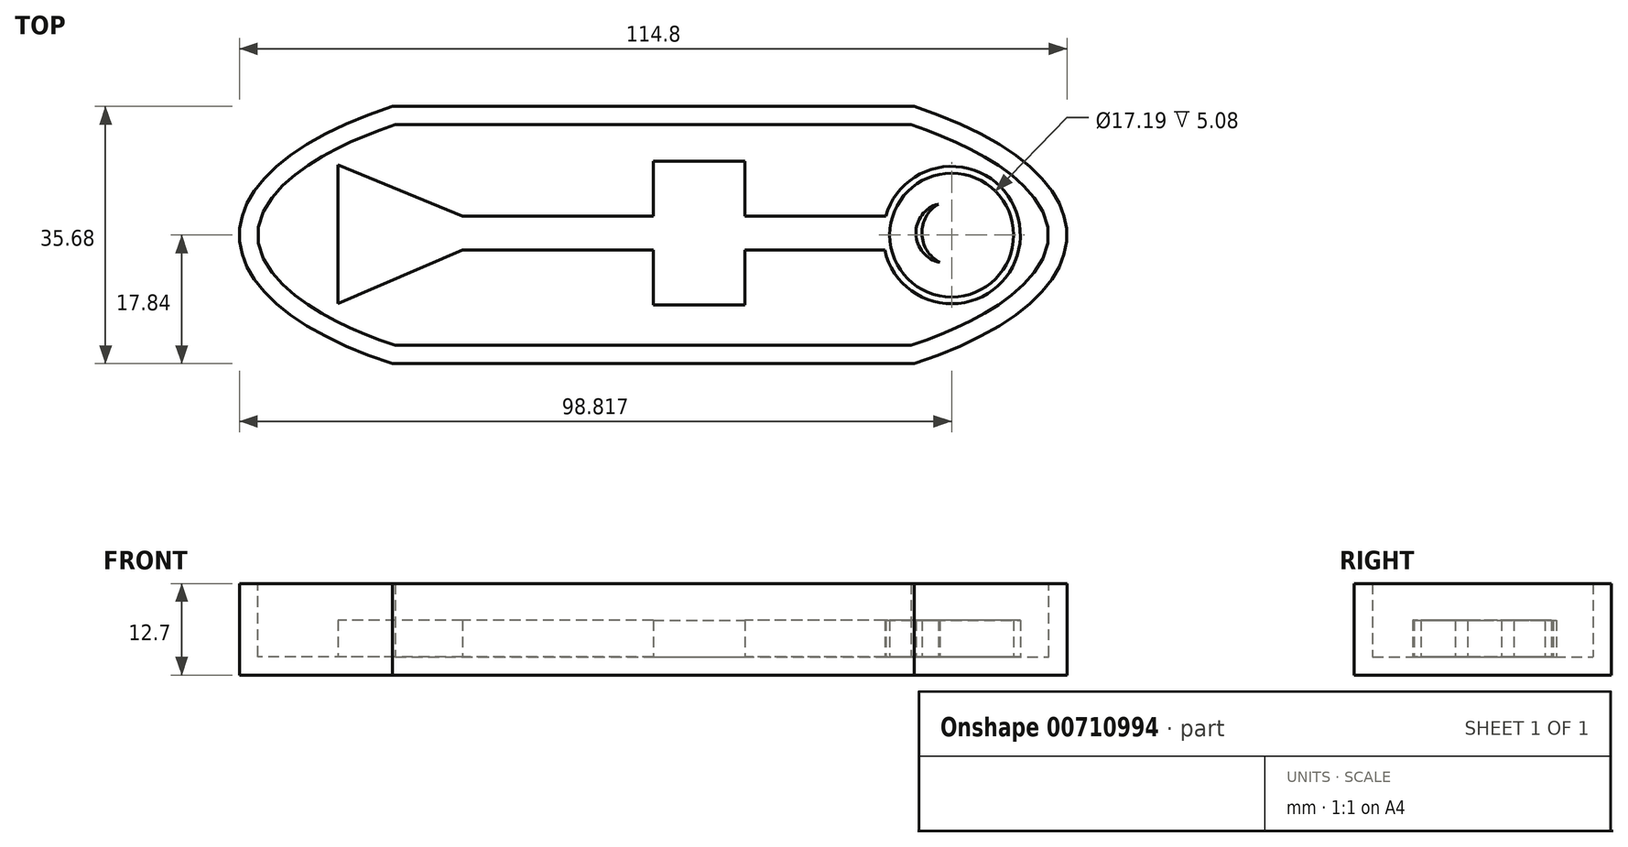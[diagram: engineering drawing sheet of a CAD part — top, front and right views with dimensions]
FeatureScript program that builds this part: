
annotation { "Feature Type Name" : "Feature", "Feature Type Description" : "" }
export const myFeature = defineFeature(function(context is Context, id is Id, definition is map)
    precondition{}
    {
        {
            var Q0;
            Q0=qCreatedBy(makeId("Top.planeOp"),FACE);
            var sketch = newSketch(context, id + "F0", { "sketchPlane" : qUnion([Q0])});
            skEllipticalArc(sketch, "E0", {});
            skLineSegment(sketch, "E1", {"start": v(-36.2, -17.84) * mm, "end": v(36.2, -17.84) * mm});
            skLineSegment(sketch, "E2", {"start": v(-36.2, 17.84) * mm, "end": v(36.2, 17.84) * mm});
            skEllipticalArc(sketch, "E3.trimOffspring", {});
            const initialGuessF0  = {"E0": [0, 0, -1, 0, 0.05740329623222351, 0.022988312008879238, 2.252938890638711, 4.030246416540875], "E3.trimOffspring": [0, 0, -1, 0, 0.05740329623222351, 0.022988312008879238, 5.394531544228505, 0.888653762951082]};
            skSetInitialGuess(sketch, initialGuessF0);
            skSolve(sketch);
        }
        {
            var Q0;
            Q0=makeQuery(id+"F0.imprint","IMPRINT",FACE,{"disambiguationData":[TD([[makeQuery(id+"F0.imprint","IMPRINT",EDGE,{"derivedFrom":sQuery(id+"F0.wireOp",EDGE,"E0")}),1.0]])]});
            extrude(context, id + "F1", {"entities" : qUnion([Q0]), "depth" : 12.7 * mm, "offsetDistance" : 25.4 * mm});
        }
        {
            var Q0;
            Q0=makeQuery(id+"F1.opExtrude","CAP_FACE",FACE,{"disambiguationData":[OSD([sQuery(id+"F0.wireOp",EDGE,"E0"),sQuery(id+"F0.wireOp",EDGE,"E1"),sQuery(id+"F0.wireOp",EDGE,"E2"),sQuery(id+"F0.wireOp",EDGE,"E3.trimOffspring")])],"isStart":false});
            shell(context, id + "F2", {"entities" : qUnion([Q0]), "thickness" : 2.54 * mm});
        }
        {
            var Q0;
            Q0=makeQuery(id+"F2.opShell","OFFSET_FACE",FACE,{"disambiguationData":[OSD([sQuery(id+"F0.wireOp",EDGE,"E0"),sQuery(id+"F0.wireOp",EDGE,"E1"),sQuery(id+"F0.wireOp",EDGE,"E2"),sQuery(id+"F0.wireOp",EDGE,"E3.trimOffspring")])]});
            var sketch = newSketch(context, id + "F3", { "sketchPlane" : qUnion([Q0])});
            skCircle(sketch, "E4", {"center": v(41.42, 0) * mm, "radius": 9.53 * mm});
            skCircle(sketch, "E5", {"center": v(41.42, 0) * mm, "radius": 8.6 * mm});
            skLineSegment(sketch, "E6", {"start": v(41.93, 8.58) * mm, "end": v(41.93, -8.58) * mm});
            skLineSegment(sketch, "E7", {"start": v(50.01, 0) * mm, "end": v(32.82, 0) * mm});
            skLineSegment(sketch, "E8", {"start": v(45.7, 7.45) * mm, "end": v(45.7, -7.45) * mm});
            skLineSegment(sketch, "E9", {"start": v(45.7, -7.45) * mm, "end": v(45.7, 7.45) * mm});
            skLineSegment(sketch, "E10", {"start": v(49.45, 3.06) * mm, "end": v(41.93, 3.06) * mm});
            skLineSegment(sketch, "E11", {"start": v(41.93, 3.06) * mm, "end": v(41.93, -3.12) * mm});
            skLineSegment(sketch, "E12", {"start": v(41.93, -3.12) * mm, "end": v(49.42, -3.12) * mm});
            skCircle(sketch, "E13", {"center": v(45.7, 3.06) * mm, "radius": 2.41 * mm});
            skCircle(sketch, "E14", {"center": v(45.7, 3.06) * mm, "radius": 1.87 * mm});
            skCircle(sketch, "E15", {"center": v(45.68, -3.12) * mm, "radius": 2.41 * mm});
            skCircle(sketch, "E16", {"center": v(45.68, -3.12) * mm, "radius": 1.87 * mm});
            skArc(sketch, "E17", {"start": v(39.57, 4.3) * mm, "mid": v(37.28, 0.2) * mm, "end": v(39.79, -3.79) * mm});
            skArc(sketch, "E18", {"start": v(39.57, 4.3) * mm, "mid": v(36.45, 0.17) * mm, "end": v(39.79, -3.79) * mm});
            skCircle(sketch, "E19", {"center": v(45.7, 3.06) * mm, "radius": 0.76 * mm});
            skCircle(sketch, "E20", {"center": v(45.68, -3.12) * mm, "radius": 0.76 * mm});
            skSolve(sketch);
        }
        {
            var Q0;
            Q0 = qSketchRegion(id + "F3", true);
            var Q1;
            {var subQ0=sQuery(id+"F3.wireOp",EDGE,"E14");var subQ1=sQuery(id+"F3.wireOp",EDGE,"E9");var subQ2=makeQuery(id+"F3.imprint","INTERSECT",VERTEX,{"disambiguationData":[OD(1.0)],"derivedFrom":[subQ1,subQ0]});Q1=makeQuery(id+"F3.imprint","IMPRINT",FACE,{"disambiguationData":[TD([[makeQuery(id+"F3.imprint","IMPRINT",EDGE,{"disambiguationData":[TD([[subQ2,-1.0]])],"derivedFrom":subQ1}),-1.0]])]});}
            var Q2;
            {var subQ0=sQuery(id+"F3.wireOp",EDGE,"E14");var subQ1=sQuery(id+"F3.wireOp",EDGE,"E9");var subQ2=makeQuery(id+"F3.imprint","INTERSECT",VERTEX,{"disambiguationData":[OD(1.0)],"derivedFrom":[subQ1,subQ0]});Q2=makeQuery(id+"F3.imprint","IMPRINT",FACE,{"disambiguationData":[TD([[makeQuery(id+"F3.imprint","IMPRINT",EDGE,{"disambiguationData":[TD([[subQ2,-1.0]])],"derivedFrom":subQ1}),1.0]])]});}
            var Q3;
            {var subQ0=sQuery(id+"F3.wireOp",EDGE,"E13");var subQ1=sQuery(id+"F3.wireOp",EDGE,"E9");var subQ2=makeQuery(id+"F3.imprint","INTERSECT",VERTEX,{"disambiguationData":[OD(0.0)],"derivedFrom":[subQ1,subQ0]});Q3=makeQuery(id+"F3.imprint","IMPRINT",FACE,{"disambiguationData":[TD([[makeQuery(id+"F3.imprint","IMPRINT",EDGE,{"disambiguationData":[TD([[subQ2,-1.0]])],"derivedFrom":subQ1}),1.0]])]});}
            var Q4;
            {var subQ0=sQuery(id+"F3.wireOp",EDGE,"E13");var subQ1=sQuery(id+"F3.wireOp",EDGE,"E9");var subQ2=makeQuery(id+"F3.imprint","INTERSECT",VERTEX,{"disambiguationData":[OD(0.0)],"derivedFrom":[subQ1,subQ0]});Q4=makeQuery(id+"F3.imprint","IMPRINT",FACE,{"disambiguationData":[TD([[makeQuery(id+"F3.imprint","IMPRINT",EDGE,{"disambiguationData":[TD([[subQ2,-1.0]])],"derivedFrom":subQ1}),-1.0]])]});}
            var Q5;
            {var subQ0=sQuery(id+"F3.wireOp",EDGE,"E16");var subQ1=sQuery(id+"F3.wireOp",EDGE,"E9");var subQ2=makeQuery(id+"F3.imprint","INTERSECT",VERTEX,{"disambiguationData":[OD(1.0)],"derivedFrom":[subQ1,subQ0]});Q5=makeQuery(id+"F3.imprint","IMPRINT",FACE,{"disambiguationData":[TD([[makeQuery(id+"F3.imprint","IMPRINT",EDGE,{"disambiguationData":[TD([[subQ2,-1.0]])],"derivedFrom":subQ1}),-1.0]])]});}
            var Q6;
            {var subQ0=sQuery(id+"F3.wireOp",EDGE,"E15");var subQ1=sQuery(id+"F3.wireOp",EDGE,"E9");var subQ2=makeQuery(id+"F3.imprint","INTERSECT",VERTEX,{"disambiguationData":[OD(0.0)],"derivedFrom":[subQ1,subQ0]});Q6=makeQuery(id+"F3.imprint","IMPRINT",FACE,{"disambiguationData":[TD([[makeQuery(id+"F3.imprint","IMPRINT",EDGE,{"disambiguationData":[TD([[subQ2,-1.0]])],"derivedFrom":subQ1}),-1.0]])]});}
            var Q7;
            {var subQ0=sQuery(id+"F3.wireOp",EDGE,"E15");var subQ1=sQuery(id+"F3.wireOp",EDGE,"E9");var subQ2=makeQuery(id+"F3.imprint","INTERSECT",VERTEX,{"disambiguationData":[OD(0.0)],"derivedFrom":[subQ1,subQ0]});Q7=makeQuery(id+"F3.imprint","IMPRINT",FACE,{"disambiguationData":[TD([[makeQuery(id+"F3.imprint","IMPRINT",EDGE,{"disambiguationData":[TD([[subQ2,-1.0]])],"derivedFrom":subQ1}),1.0]])]});}
            var Q8;
            {var subQ0=sQuery(id+"F3.wireOp",EDGE,"E16");var subQ1=sQuery(id+"F3.wireOp",EDGE,"E9");var subQ2=makeQuery(id+"F3.imprint","INTERSECT",VERTEX,{"disambiguationData":[OD(1.0)],"derivedFrom":[subQ1,subQ0]});Q8=makeQuery(id+"F3.imprint","IMPRINT",FACE,{"disambiguationData":[TD([[makeQuery(id+"F3.imprint","IMPRINT",EDGE,{"disambiguationData":[TD([[subQ2,-1.0]])],"derivedFrom":subQ1}),1.0]])]});}
            var Q9;
            {var subQ0=sQuery(id+"F3.wireOp",EDGE,"E10");var subQ1=sQuery(id+"F3.wireOp",EDGE,"E9");var subQ2=makeQuery(id+"F3.imprint","INTERSECT",VERTEX,{"derivedFrom":[subQ1,subQ0]});Q9=makeQuery(id+"F3.imprint","IMPRINT",FACE,{"disambiguationData":[TD([[makeQuery(id+"F3.imprint","IMPRINT",EDGE,{"disambiguationData":[TD([[subQ2,-1.0]])],"derivedFrom":subQ1}),1.0]])]});}
            var Q10;
            {var subQ0=sQuery(id+"F3.wireOp",EDGE,"E10");var subQ1=sQuery(id+"F3.wireOp",EDGE,"E9");var subQ2=makeQuery(id+"F3.imprint","INTERSECT",VERTEX,{"derivedFrom":[subQ1,subQ0]});Q10=makeQuery(id+"F3.imprint","IMPRINT",FACE,{"disambiguationData":[TD([[makeQuery(id+"F3.imprint","IMPRINT",EDGE,{"disambiguationData":[TD([[subQ2,-1.0]])],"derivedFrom":subQ1}),-1.0]])]});}
            var Q11;
            {var subQ0=sQuery(id+"F3.wireOp",EDGE,"E19");var subQ1=sQuery(id+"F3.wireOp",EDGE,"E9");var subQ2=makeQuery(id+"F3.imprint","INTERSECT",VERTEX,{"disambiguationData":[OD(0.0)],"derivedFrom":[subQ1,subQ0]});Q11=makeQuery(id+"F3.imprint","IMPRINT",FACE,{"disambiguationData":[TD([[makeQuery(id+"F3.imprint","IMPRINT",EDGE,{"disambiguationData":[TD([[subQ2,-1.0]])],"derivedFrom":subQ1}),-1.0]])]});}
            var Q12;
            {var subQ0=sQuery(id+"F3.wireOp",EDGE,"E19");var subQ1=sQuery(id+"F3.wireOp",EDGE,"E9");var subQ2=makeQuery(id+"F3.imprint","INTERSECT",VERTEX,{"disambiguationData":[OD(0.0)],"derivedFrom":[subQ1,subQ0]});Q12=makeQuery(id+"F3.imprint","IMPRINT",FACE,{"disambiguationData":[TD([[makeQuery(id+"F3.imprint","IMPRINT",EDGE,{"disambiguationData":[TD([[subQ2,-1.0]])],"derivedFrom":subQ1}),1.0]])]});}
            var Q13;
            {var subQ0=sQuery(id+"F3.wireOp",EDGE,"E12");var subQ1=sQuery(id+"F3.wireOp",EDGE,"E9");var subQ2=makeQuery(id+"F3.imprint","INTERSECT",VERTEX,{"derivedFrom":[subQ1,subQ0]});Q13=makeQuery(id+"F3.imprint","IMPRINT",FACE,{"disambiguationData":[TD([[makeQuery(id+"F3.imprint","IMPRINT",EDGE,{"disambiguationData":[TD([[subQ2,-1.0]])],"derivedFrom":subQ1}),1.0]])]});}
            var Q14;
            {var subQ0=sQuery(id+"F3.wireOp",EDGE,"E20");var subQ1=sQuery(id+"F3.wireOp",EDGE,"E9");var subQ2=makeQuery(id+"F3.imprint","INTERSECT",VERTEX,{"disambiguationData":[OD(0.0)],"derivedFrom":[subQ1,subQ0]});Q14=makeQuery(id+"F3.imprint","IMPRINT",FACE,{"disambiguationData":[TD([[makeQuery(id+"F3.imprint","IMPRINT",EDGE,{"disambiguationData":[TD([[subQ2,-1.0]])],"derivedFrom":subQ1}),1.0]])]});}
            var Q15;
            {var subQ0=sQuery(id+"F3.wireOp",EDGE,"E20");var subQ1=sQuery(id+"F3.wireOp",EDGE,"E9");var subQ2=makeQuery(id+"F3.imprint","INTERSECT",VERTEX,{"disambiguationData":[OD(0.0)],"derivedFrom":[subQ1,subQ0]});Q15=makeQuery(id+"F3.imprint","IMPRINT",FACE,{"disambiguationData":[TD([[makeQuery(id+"F3.imprint","IMPRINT",EDGE,{"disambiguationData":[TD([[subQ2,-1.0]])],"derivedFrom":subQ1}),-1.0]])]});}
            var Q16;
            {var subQ0=sQuery(id+"F3.wireOp",EDGE,"E12");var subQ1=sQuery(id+"F3.wireOp",EDGE,"E9");var subQ2=makeQuery(id+"F3.imprint","INTERSECT",VERTEX,{"derivedFrom":[subQ1,subQ0]});Q16=makeQuery(id+"F3.imprint","IMPRINT",FACE,{"disambiguationData":[TD([[makeQuery(id+"F3.imprint","IMPRINT",EDGE,{"disambiguationData":[TD([[subQ2,-1.0]])],"derivedFrom":subQ1}),-1.0]])]});}
            var Q17;
            {var subQ0=sQuery(id+"F3.wireOp",EDGE,"E17");var subQ1=sQuery(id+"F3.wireOp",EDGE,"E7");var subQ2=makeQuery(id+"F3.imprint","INTERSECT",VERTEX,{"derivedFrom":[subQ1,subQ0]});Q17=makeQuery(id+"F3.imprint","IMPRINT",FACE,{"disambiguationData":[TD([[makeQuery(id+"F3.imprint","IMPRINT",EDGE,{"disambiguationData":[TD([[subQ2,-1.0]])],"derivedFrom":subQ1}),-1.0]])]});}
            var Q18;
            {var subQ0=sQuery(id+"F3.wireOp",EDGE,"E17");var subQ1=sQuery(id+"F3.wireOp",EDGE,"E7");var subQ2=makeQuery(id+"F3.imprint","INTERSECT",VERTEX,{"derivedFrom":[subQ1,subQ0]});Q18=makeQuery(id+"F3.imprint","IMPRINT",FACE,{"disambiguationData":[TD([[makeQuery(id+"F3.imprint","IMPRINT",EDGE,{"disambiguationData":[TD([[subQ2,-1.0]])],"derivedFrom":subQ1}),1.0]])]});}
            extrude(context, id + "F4", {"entities" : qUnion([Q0, Q1, Q2, Q3, Q4, Q5, Q6, Q7, Q8, Q9, Q10, Q11, Q12, Q13, Q14, Q15, Q16, Q17, Q18]), "operationType" : NewBodyOperationType.ADD, "depth" : 5.08 * mm, "offsetDistance" : 25.4 * mm});
        }
        {
            var Q0;
            {var subQ0=sQuery(id+"F0.wireOp",EDGE,"E3.trimOffspring");var subQ1=sQuery(id+"F0.wireOp",EDGE,"E2");var subQ2=sQuery(id+"F0.wireOp",EDGE,"E1");var subQ3=sQuery(id+"F0.wireOp",EDGE,"E0");Q0=makeQuery(id+"F4.boolean.opBoolean","SPLIT",FACE,{"disambiguationData":[TD([makeQuery(id+"F2.opShell","OFFSET_FACE",FACE,{"disambiguationData":[OSD([subQ3])]})])],"derivedFrom":makeQuery(id+"F2.opShell","OFFSET_FACE",FACE,{"disambiguationData":[OSD([subQ3,subQ2,subQ1,subQ0])]})});}
            var sketch = newSketch(context, id + "F5", { "sketchPlane" : qUnion([Q0])});
            skLineSegment(sketch, "E21", {"start": v(33.96, 5.93) * mm, "end": v(-26.44, 5.93) * mm});
            skLineSegment(sketch, "E22", {"start": v(-26.44, 5.93) * mm, "end": v(-26.44, -5.51) * mm});
            skLineSegment(sketch, "E23", {"start": v(-26.44, -5.51) * mm, "end": v(35.78, -5.51) * mm});
            skLineSegment(sketch, "E24", {"start": v(35.78, -5.51) * mm, "end": v(-26.44, -5.51) * mm});
            skLineSegment(sketch, "E25.bottom", {"start": v(32.26, 2.61) * mm, "end": v(-26.44, 2.61) * mm});
            skLineSegment(sketch, "E25.top", {"start": v(32.26, -2.1) * mm, "end": v(-26.44, -2.1) * mm});
            skLineSegment(sketch, "E25.left", {"start": v(32.26, 2.61) * mm, "end": v(32.26, -2.1) * mm});
            skLineSegment(sketch, "E25.right", {"start": v(-26.44, 2.61) * mm, "end": v(-26.44, -2.1) * mm});
            skSolve(sketch);
        }
        {
            var Q0;
            Q0 = qSketchRegion(id + "F5", true);
            extrude(context, id + "F6", {"entities" : qUnion([Q0]), "operationType" : NewBodyOperationType.ADD, "depth" : 5.08 * mm, "offsetDistance" : 25.4 * mm});
        }
        {
            var Q0;
            {var subQ0=sQuery(id+"F0.wireOp",EDGE,"E3.trimOffspring");var subQ1=sQuery(id+"F0.wireOp",EDGE,"E2");var subQ2=sQuery(id+"F0.wireOp",EDGE,"E1");var subQ3=sQuery(id+"F0.wireOp",EDGE,"E0");Q0=makeQuery(id+"F4.boolean.opBoolean","SPLIT",FACE,{"disambiguationData":[TD([makeQuery(id+"F2.opShell","OFFSET_FACE",FACE,{"disambiguationData":[OSD([subQ3])]})])],"derivedFrom":makeQuery(id+"F2.opShell","OFFSET_FACE",FACE,{"disambiguationData":[OSD([subQ3,subQ2,subQ1,subQ0])]})});}
            var sketch = newSketch(context, id + "F7", { "sketchPlane" : qUnion([Q0])});
            skLineSegment(sketch, "E26", {"start": v(-26.44, 2.61) * mm, "end": v(-43.7, 9.75) * mm});
            skLineSegment(sketch, "E27", {"start": v(-43.7, 9.75) * mm, "end": v(-43.7, -7.77) * mm});
            skLineSegment(sketch, "E28", {"start": v(-43.7, -7.77) * mm, "end": v(-26.44, -2.1) * mm});
            skLineSegment(sketch, "E29", {"start": v(-26.44, -2.1) * mm, "end": v(-43.7, -9.51) * mm});
            skLineSegment(sketch, "E30", {"start": v(-43.7, -9.51) * mm, "end": v(-43.7, -7.77) * mm});
            skSolve(sketch);
        }
        {
            var Q0;
            Q0 = qSketchRegion(id + "F7", true);
            var Q1;
            Q1=makeQuery(id+"F7.imprint","IMPRINT",FACE,{"disambiguationData":[TD([[makeQuery(id+"F7.imprint","IMPRINT",EDGE,{"derivedFrom":sQuery(id+"F7.wireOp",EDGE,"E26")}),1.0]])]});
            extrude(context, id + "F8", {"entities" : qUnion([Q0, Q1]), "operationType" : NewBodyOperationType.ADD, "depth" : 5.08 * mm, "offsetDistance" : 25.4 * mm});
        }
        {
            var Q0;
            {var subQ0=sQuery(id+"F0.wireOp",EDGE,"E3.trimOffspring");var subQ1=sQuery(id+"F0.wireOp",EDGE,"E2");var subQ2=sQuery(id+"F0.wireOp",EDGE,"E1");var subQ3=sQuery(id+"F0.wireOp",EDGE,"E0");Q0=makeQuery(id+"F4.boolean.opBoolean","SPLIT",FACE,{"disambiguationData":[TD([makeQuery(id+"F2.opShell","OFFSET_FACE",FACE,{"disambiguationData":[OSD([subQ3])]})])],"derivedFrom":makeQuery(id+"F2.opShell","OFFSET_FACE",FACE,{"disambiguationData":[OSD([subQ3,subQ2,subQ1,subQ0])]})});}
            var sketch = newSketch(context, id + "F9", { "sketchPlane" : qUnion([Q0])});
            skLineSegment(sketch, "E31", {"start": v(0, 15.3) * mm, "end": v(0, -15.3) * mm});
            skLineSegment(sketch, "E32", {"start": v(0, -15.3) * mm, "end": v(0, 15.3) * mm});
            skLineSegment(sketch, "E33.bottom", {"start": v(0, 2.61) * mm, "end": v(12.7, 2.61) * mm});
            skLineSegment(sketch, "E33.top", {"start": v(0, 10.23) * mm, "end": v(12.7, 10.23) * mm});
            skLineSegment(sketch, "E33.left", {"start": v(0, 2.61) * mm, "end": v(0, 10.23) * mm});
            skLineSegment(sketch, "E33.right", {"start": v(12.7, 2.61) * mm, "end": v(12.7, 10.23) * mm});
            skLineSegment(sketch, "E34.bottom", {"start": v(0, -2.1) * mm, "end": v(12.7, -2.1) * mm});
            skLineSegment(sketch, "E34.top", {"start": v(0, -9.72) * mm, "end": v(12.7, -9.72) * mm});
            skLineSegment(sketch, "E34.left", {"start": v(0, -2.1) * mm, "end": v(0, -9.72) * mm});
            skLineSegment(sketch, "E34.right", {"start": v(12.7, -2.1) * mm, "end": v(12.7, -9.72) * mm});
            skSolve(sketch);
        }
        {
            var Q0;
            Q0 = qSketchRegion(id + "F9", true);
            extrude(context, id + "F10", {"entities" : qUnion([Q0]), "operationType" : NewBodyOperationType.ADD, "depth" : 5.08 * mm, "offsetDistance" : 25.4 * mm});
        }
    });
